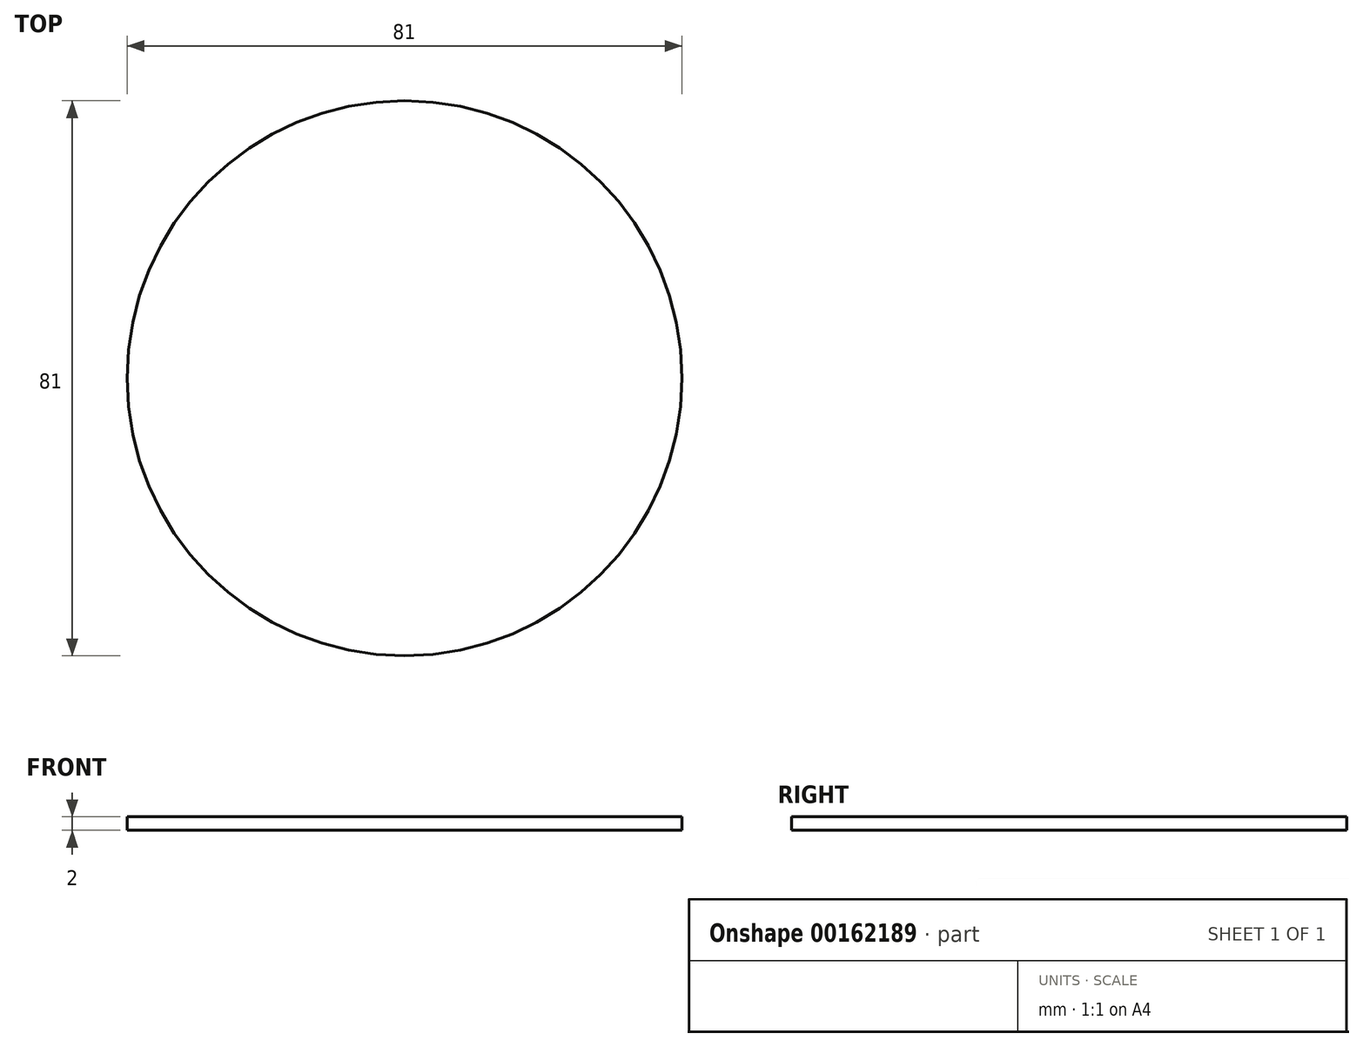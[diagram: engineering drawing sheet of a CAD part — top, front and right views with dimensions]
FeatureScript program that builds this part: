
annotation { "Feature Type Name" : "Feature", "Feature Type Description" : "" }
export const myFeature = defineFeature(function(context is Context, id is Id, definition is map)
    precondition{}
    {
        {
            var Q0;
            Q0=qCreatedBy(makeId("Top.planeOp"),FACE);
            var sketch = newSketch(context, id + "F0", { "sketchPlane" : qUnion([Q0])});
            skCircle(sketch, "E0", {"center": v(0, 0) * mm, "radius": 40.5 * mm});
            skSolve(sketch);
        }
        {
            var Q0;
            Q0=makeQuery(id+"F0.imprint","IMPRINT",FACE,{"disambiguationData":[TD([[makeQuery(id+"F0.imprint","IMPRINT",EDGE,{"derivedFrom":sQuery(id+"F0.wireOp",EDGE,"E0")}),1.0]])]});
            extrude(context, id + "F1", {"entities" : qUnion([Q0]), "depth" : 2 * mm, "offsetDistance" : 25 * mm});
        }
    });
